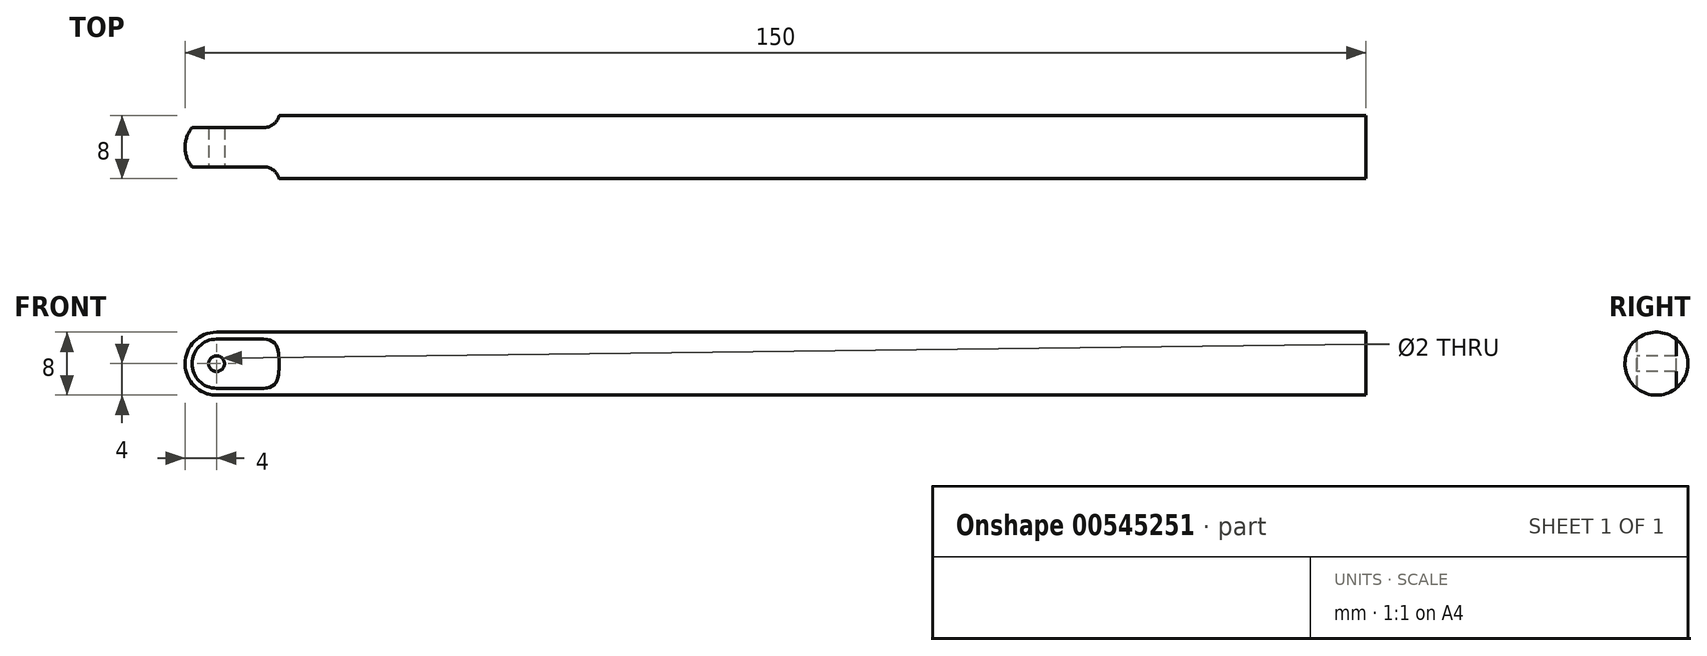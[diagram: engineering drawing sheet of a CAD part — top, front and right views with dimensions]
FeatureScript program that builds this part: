
annotation { "Feature Type Name" : "Feature", "Feature Type Description" : "" }
export const myFeature = defineFeature(function(context is Context, id is Id, definition is map)
    precondition{}
    {
        {
            var Q0;
            Q0=qCreatedBy(makeId("Right.planeOp"),FACE);
            var sketch = newSketch(context, id + "F0", { "sketchPlane" : qUnion([Q0])});
            skCircle(sketch, "E0", {"center": v(0, 0) * mm, "radius": 4 * mm});
            skSolve(sketch);
        }
        {
            var Q0;
            Q0=makeQuery(id+"F0.imprint","IMPRINT",FACE,{"disambiguationData":[TD([[makeQuery(id+"F0.imprint","IMPRINT",EDGE,{"derivedFrom":sQuery(id+"F0.wireOp",EDGE,"E0")}),1.0]])]});
            extrude(context, id + "F1", {"entities" : qUnion([Q0]), "depth" : 150 * mm, "offsetDistance" : 25.4 * mm});
        }
        {
            var Q0;
            Q0=makeQuery(id+"F1.opExtrude","CAP_FACE",FACE,{"disambiguationData":[OSD([sQuery(id+"F0.wireOp",EDGE,"E0")])],"isStart":true});
            var sketch = newSketch(context, id + "F2", { "sketchPlane" : qUnion([Q0])});
            skArc(sketch, "E1", {"start": v(-2.5, 3.12) * mm, "mid": v(-4, 0) * mm, "end": v(-2.5, -3.12) * mm});
            skLineSegment(sketch, "E2.left", {"start": v(2.5, -3.12) * mm, "end": v(2.5, 3.12) * mm});
            skLineSegment(sketch, "E2.right", {"start": v(-2.5, -3.12) * mm, "end": v(-2.5, 3.12) * mm});
            skPoint(sketch, "E3.orphan", {"position": v(-2.5, 1.71) * mm});
            skPoint(sketch, "E4.orphan", {"position": v(2.5, 1.7) * mm});
            skArc(sketch, "E5.trimOffspring", {"start": v(2.5, -3.12) * mm, "mid": v(4, 0) * mm, "end": v(2.5, 3.12) * mm});
            skPoint(sketch, "E2.bottom.end.orphan", {"position": v(-2.5, -1.7) * mm});
            skPoint(sketch, "E6.orphan", {"position": v(2.5, -1.71) * mm});
            skSolve(sketch);
        }
        {
            var Q0;
            Q0=makeQuery(id+"F2.imprint","IMPRINT",FACE,{"disambiguationData":[TD([[makeQuery(id+"F2.imprint","IMPRINT",EDGE,{"derivedFrom":sQuery(id+"F2.wireOp",EDGE,"E1")}),-1.0]])]});
            var Q1;
            Q1=makeQuery(id+"F2.imprint","IMPRINT",FACE,{"disambiguationData":[TD([[makeQuery(id+"F2.imprint","IMPRINT",EDGE,{"derivedFrom":sQuery(id+"F2.wireOp",EDGE,"E2.left")}),-1.0]])]});
            extrude(context, id + "F3", {"entities" : qUnion([Q0, Q1]), "operationType" : NewBodyOperationType.REMOVE, "oppositeDirection" : true, "depth" : 12 * mm, "offsetDistance" : 25.4 * mm});
        }
        {
            var Q0;
            Q0=makeQuery(id+"F3.boolean.opBoolean","SPLIT",EDGE,{"disambiguationData":[OD(1.0)],"derivedFrom":makeQuery(id+"F1.opExtrude","CAP_EDGE",EDGE,{"disambiguationData":[OSD([sQuery(id+"F0.wireOp",EDGE,"E0")])],"isStart":true})});
            fillet(context, id + "F4", {"entities" : qUnion([Q0]), "radius" : 4 * mm, "tangentPropagation" : true, "allowEdgeOverflow" : false});
        }
        {
            var Q0;
            Q0=makeQuery(id+"F3.boolean.opBoolean","COPY",EDGE,{"derivedFrom":makeQuery(id+"F3.opExtrude","CAP_EDGE",EDGE,{"disambiguationData":[OSD([sQuery(id+"F2.wireOp",EDGE,"E2.right")])],"isStart":false})});
            fillet(context, id + "F5", {"entities" : qUnion([Q0]), "radius" : 2 * mm, "tangentPropagation" : true, "allowEdgeOverflow" : false});
        }
        {
            var Q0;
            Q0=makeQuery(id+"F3.boolean.opBoolean","COPY",EDGE,{"derivedFrom":makeQuery(id+"F3.opExtrude","CAP_EDGE",EDGE,{"disambiguationData":[OSD([sQuery(id+"F2.wireOp",EDGE,"E2.left")])],"isStart":false})});
            fillet(context, id + "F6", {"entities" : qUnion([Q0]), "radius" : 2 * mm, "tangentPropagation" : true, "allowEdgeOverflow" : false});
        }
        {
            var Q0;
            Q0=makeQuery(id+"F3.boolean.opBoolean","COPY",FACE,{"derivedFrom":makeQuery(id+"F3.opExtrude","SWEPT_FACE",FACE,{"disambiguationData":[OSD([sQuery(id+"F2.wireOp",EDGE,"E2.left")])]})});
            var sketch = newSketch(context, id + "F7", { "sketchPlane" : qUnion([Q0])});
            skPoint(sketch, "E7", {"position": v(4, 0) * mm});
            skSolve(sketch);
        }
        {
            var Q0;
            Q0=sQuery(id+"F7.wireOp",VERTEX,"E7");
            var Q1;
            Q1=makeQuery(id+"F1.opExtrude","SWEPT_BODY",BODY,{"disambiguationData":[OSD([sQuery(id+"F0.wireOp",EDGE,"E0")])]});
            hole(context, id + "F8", {"style" : HoleStyle.SIMPLE, "endStyle" : HoleEndStyle.THROUGH, "holeDiameter" : 2 * mm, "isTappedThrough" : true, "tappedDepth" : 12.7 * mm, "tapClearance" : 3, "startFromSketch" : true, "locations" : qUnion([Q0]), "scope" : qUnion([Q1])});
        }
    });
